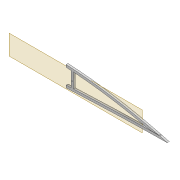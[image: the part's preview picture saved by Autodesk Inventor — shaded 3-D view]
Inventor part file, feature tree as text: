
AUTODESK INVENTOR PART (.ipt)
format: ipt  version: 2022 (Build 260153000, 153)  size: 361,984 bytes
history: native  units: mm
features: extrude x7, sketch x7, projected_geometry x5, shell x1, fillet x1, plane x1
ambient origin geometry x8: Origin, YZ Plane, XZ Plane, XY Plane, X Axis, Y Axis, Z Axis, Center Point
bodies: Solid1 (feature_tree)
feature tree (22):
  extrude  "Extrusion1"  Depth=5.0mm
  shell  "Shell1"  Thickness=2.0mm
  extrude  "Extrusion8"  Depth=5.9mm
  extrude  "Extrusion3"  Depth=10.0mm TaperAngle=0.0deg
  extrude  "Extrusion4"  Depth=2.0mm
  fillet  "Fillet1"  Radius=5.0mm
  extrude  "Extrusion5"  Depth=2.5mm
  plane  "Work Plane2"
  extrude  "Extrusion9"  Depth=1.6mm
  extrude  "Extrusion10"  Depth=67.0mm
  sketch  "Sketch3"  dims[d0=4.0mm d1=0.0mm d2=5.0mm d7=2.0mm]
  sketch  "Sketch8"  dims[d8=2.0mm d9=5.9mm]
  sketch  "Sketch9"  dims[d13=10.0mm d14=0.0mm d16=10.0mm d17=0.0mm]
  sketch  "Sketch10"  dims[d22=4.0mm d23=0.0mm d31=2.0mm d32=5.0mm]
  projected_geometry  "Projected Loop4"
  projected_geometry  "Projected Loop10"
  sketch  "Sketch24"  dims[d34=1.6mm d35=2.5mm]
  projected_geometry  "Projected Loop11"
  projected_geometry  "Projected Loop12"
  sketch  "Sketch26"  dims[d37=5.0mm d38=1.6mm]
  projected_geometry  "Projected Loop13"
  sketch  "Sketch27"  dims[d40=2.5mm d62=67.0mm d63=6.0mm d64=4.0mm d65=0.0mm d66=3.0mm d67=12.0mm d68=75.0mm d69=20.0mm d70=0.5mm d71=10.0mm d72=0.0mm d73=10.0mm d74=0.0mm]
